# Revit family: TMI_M3016-Music_Wire Grille Doors1
name_source: partatom
category: Casework
revit_build: Autodesk Revit 2016 (Build: 20150220_1215(x64)
units: mm (PartAtom-declared; Revit-internal decimal feet)

## family parameters
Always vertical = Yes
Cut with Voids When Loaded = No
OmniClass Number = 23.40.35.14.11
OmniClass Title = Modular Casework
Room Calculation Point = No
Shared = No
Work Plane-Based = No

## types (2) — shared parameters
Cabinet Finish = Plastic Laminate
Casework Back Thickness = 1/2"
Casework Thickness = 3/4"
Height = 84 1/2"
Interior Finish = <By Category>
Manufacturer = TMI Systems Corporation
Model = M3016/M5016
Shelf Thickness = 1 1/8"
Toe Kick Depth = 2"
Toe Kick Height = 4"
URL = www.tmisystems.com
Width = 27"

## per-type parameters (varying)
| type | Depth | Description |
| 27" x 84-1/2" x 29" | 29" | Alto Saxophone, Cornet, Trumpet *Top*, Alto Horn, French Horn, Share Drum *Bottom* |
| 27" x 84-1/2" x 39" | 39" | Alto Clarinet, Bassoon, Bass Clarinet, Tenor Saxophone, Trombone, Violin, Viola *Top* Piccolo, Baritone, Euphonium, Mellophone *Bottom* |

## geometry (parser evidence)
native form markers: Blend x6, Sweep x19
no freeform markers — native parametric forms only
